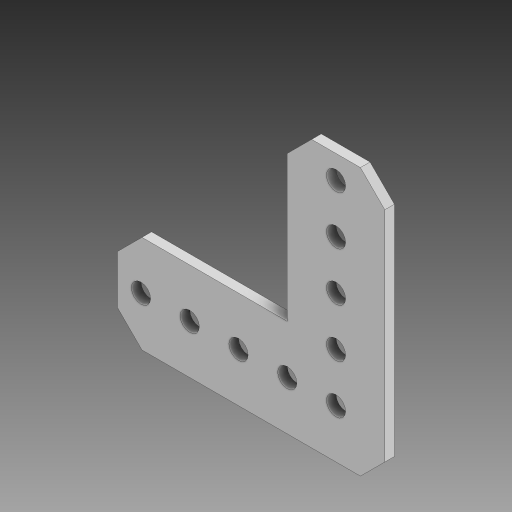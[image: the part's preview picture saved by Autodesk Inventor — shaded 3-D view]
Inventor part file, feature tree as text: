
AUTODESK INVENTOR PART (.ipt)
format: ipt  version: 2023.4 (Build 274418000, 418)  size: 120,832 bytes
history: native  units: in
note: dims shown in document units (in); Inventor stores cm internally (conversion verified against a paired STEP export)
features: chamfer x1
ambient origin geometry x8: Origin, YZ Plane, XZ Plane, XY Plane, X Axis, Y Axis, Z Axis, Center Point
bodies: Solid1 (feature_tree)
feature tree (1):
  chamfer  "Chamfer1"  [1 undecoded]
note: 1 required parameter value undecoded (feature->parameter linkage not recoverable at this tier; creation-order binding heuristic only, values carry confidence <= 0.55)
